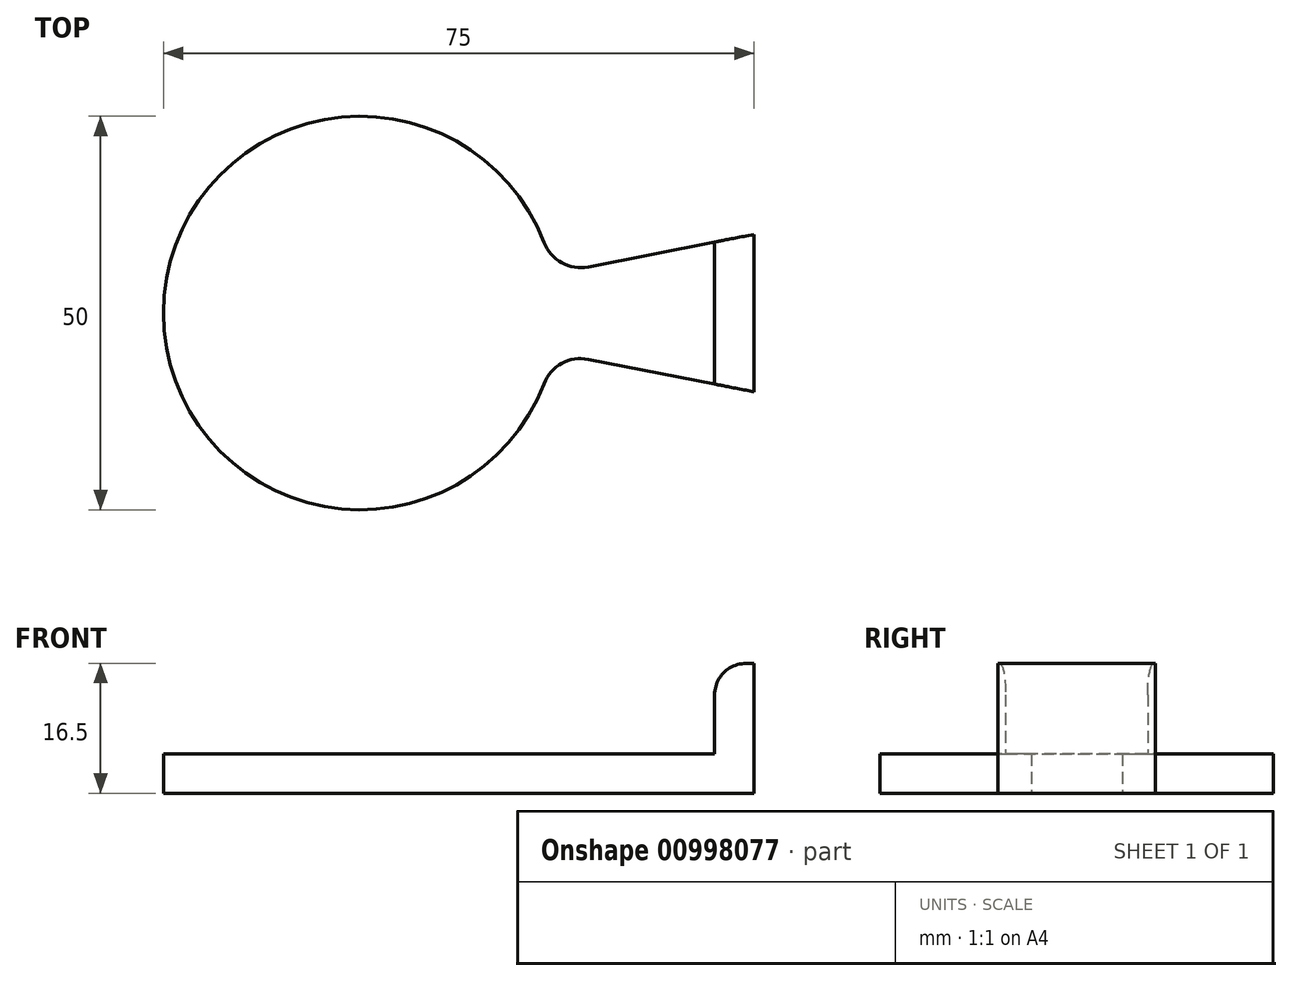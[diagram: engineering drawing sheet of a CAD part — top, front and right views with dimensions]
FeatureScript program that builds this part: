
annotation { "Feature Type Name" : "Feature", "Feature Type Description" : "" }
export const myFeature = defineFeature(function(context is Context, id is Id, definition is map)
    precondition{}
    {
        {
            var Q0;
            Q0=qCreatedBy(makeId("Top.planeOp"),FACE);
            var sketch = newSketch(context, id + "F0", { "sketchPlane" : qUnion([Q0])});
            skArc(sketch, "E0", {"start": v(24.5, 5) * mm, "mid": v(-25, 0) * mm, "end": v(24.5, -5) * mm});
            skLineSegment(sketch, "E1", {"start": v(24.5, 5) * mm, "end": v(50, 10) * mm});
            skLineSegment(sketch, "E2", {"start": v(50, 10) * mm, "end": v(50, -10) * mm});
            skLineSegment(sketch, "E3", {"start": v(50, -10) * mm, "end": v(24.5, -5) * mm});
            skSolve(sketch);
        }
        {
            var Q0;
            Q0 = qSketchRegion(id + "F0", true);
            extrude(context, id + "F1", {"entities" : qUnion([Q0]), "depth" : 5 * mm, "offsetDistance" : 25 * mm});
        }
        {
            var Q0;
            Q0=makeQuery(id+"F1.opExtrude","CAP_FACE",FACE,{"disambiguationData":[OSD([sQuery(id+"F0.wireOp",EDGE,"E0"),sQuery(id+"F0.wireOp",EDGE,"kwB8ffBj-g11f-9dtH-zG7g-A9r3zUjhK8gp"),sQuery(id+"F0.wireOp",EDGE,"kyTlqcJt-IFEi-DAoD-bBBB-bgiWYzslx68q"),sQuery(id+"F0.wireOp",EDGE,"TjZd7Ko3-Wg3r-GU8W-SGQQ-2vY92HTyocck")])],"isStart":false});
            var sketch = newSketch(context, id + "F2", { "sketchPlane" : qUnion([Q0])});
            skLineSegment(sketch, "E4", {"start": v(50, 10) * mm, "end": v(50, -10) * mm});
            skLineSegment(sketch, "E5", {"start": v(50, -10) * mm, "end": v(45, -9.02) * mm});
            skLineSegment(sketch, "E6", {"start": v(45, -9.02) * mm, "end": v(45, 9.02) * mm});
            skLineSegment(sketch, "E7", {"start": v(45, 9.02) * mm, "end": v(50, 10) * mm});
            skSolve(sketch);
        }
        {
            var Q0;
            Q0 = qSketchRegion(id + "F2", true);
            extrude(context, id + "F3", {"entities" : qUnion([Q0]), "operationType" : NewBodyOperationType.ADD, "depth" : 11.5 * mm, "offsetDistance" : 25 * mm});
        }
        {
            var Q0;
            Q0=makeQuery(id+"F1.opExtrude","SWEPT_EDGE",EDGE,{"disambiguationData":[OSD([sQuery(id+"F0.wireOp",EDGE,"E0"),sQuery(id+"F0.wireOp",EDGE,"E1")])]});
            var Q1;
            Q1=makeQuery(id+"F1.opExtrude","SWEPT_EDGE",EDGE,{"disambiguationData":[OSD([sQuery(id+"F0.wireOp",EDGE,"E0"),sQuery(id+"F0.wireOp",EDGE,"E3")])]});
            var Q2;
            Q2=makeQuery(id+"F3.opExtrude","CAP_EDGE",EDGE,{"disambiguationData":[OSD([sQuery(id+"F2.wireOp",EDGE,"E6")])],"isStart":true});
            fillet(context, id + "F4", {"entities" : qUnion([Q0, Q1, Q2]), "radius" : 5 * mm, "tangentPropagation" : true, "allowEdgeOverflow" : false});
        }
        {
            var Q0;
            Q0=makeQuery(id+"F3.opExtrude","CAP_EDGE",EDGE,{"disambiguationData":[OSD([sQuery(id+"F2.wireOp",EDGE,"E6")])],"isStart":false});
            fillet(context, id + "F5", {"entities" : qUnion([Q0]), "radius" : 4 * mm, "tangentPropagation" : true, "allowEdgeOverflow" : false});
        }
    });
